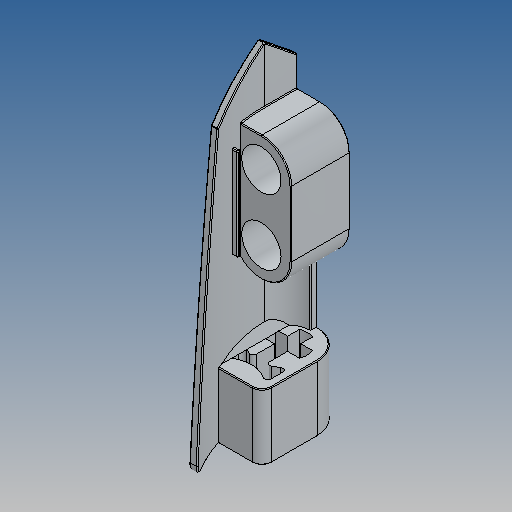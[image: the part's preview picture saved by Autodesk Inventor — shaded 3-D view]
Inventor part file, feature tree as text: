
AUTODESK INVENTOR PART (.ipt)
format: ipt  version: 2025 (Build 290162010, 162A)  size: 543,744 bytes
history: native  units: in
note: dims shown in document units (in); Inventor stores cm internally (conversion verified against a paired STEP export)
features: extrude x12, sketch x4, plane x1, fillet x1
ambient origin geometry x8: Origin, YZ Plane, XZ Plane, XY Plane, X Axis, Y Axis, Z Axis, Center Point
bodies: Solid1 (feature_tree)
feature tree (18):
  sketch  "Sketch2"  dims[d3=0.315in d4=0.0in d5=0.0315in]
  extrude  "Extrusion1"  Depth=0.315in
  sketch  "Sketch3"  dims[d16=0.4724in d17=0.0in d33=0.0157in d34=0.0in]
  extrude  "Extrusion4"  Depth=0.0157in TaperAngle=0.0deg
  extrude  "Extrusion8"  Depth=0.315in
  extrude  "Extrusion7"  Depth=0.1575in
  extrude  "Extrusion29"  Depth=0.1575in
  extrude  "Extrusion30"  Depth=0.1575in
  extrude  "Extrusion23"  Depth=0.1575in
  extrude  "Extrusion24"  Depth=0.1575in
  extrude  "Extrusion25"  Depth=0.0039in
  extrude  "Extrusion26"  Depth=0.1575in TaperAngle=0.0deg
  extrude  "Extrusion27"  Depth=0.1575in TaperAngle=0.0deg
  plane  "Work Plane2"
  extrude  "Extrusion28"  Depth=0.1575in TaperAngle=0.0deg
  fillet  "Fillet2"  Radius=0.0315in
  sketch  "Sketch5"  dims[d37=0.7244in d38=0.0in d45=0.378in d46=0.315in]
  sketch  "Sketch12"  dims[d85=0.315in d86=0.252in d87=0.189in d88=0.2835in d89=0.0394in d90=0.7874in d91=0.0039in d92=0.2835in d93=0.0in d94=0.2835in d95=0.0in d96=0.2835in d97=0.0in d98=0.0315in d99=0.0in d100=0.252in d101=0.0in d102=0.0327in d103=0.0157in d104=0.0315in d105=0.4409in d106=0.0in d108=0.0039in d109=0.0157in d110=0.189in d111=0.2835in d112=0.0354in d113=0.315in d114=0.063in d115=0.0157in d116=0.3937in d117=0.0in d118=0.3937in d119=0.0in d120=0.8661in d121=0.242in d122=0.0472in d123=0.2008in d124=1.3071in d125=1.3858in d126=0.1575in d127=0.4252in d128=0.0394in]
